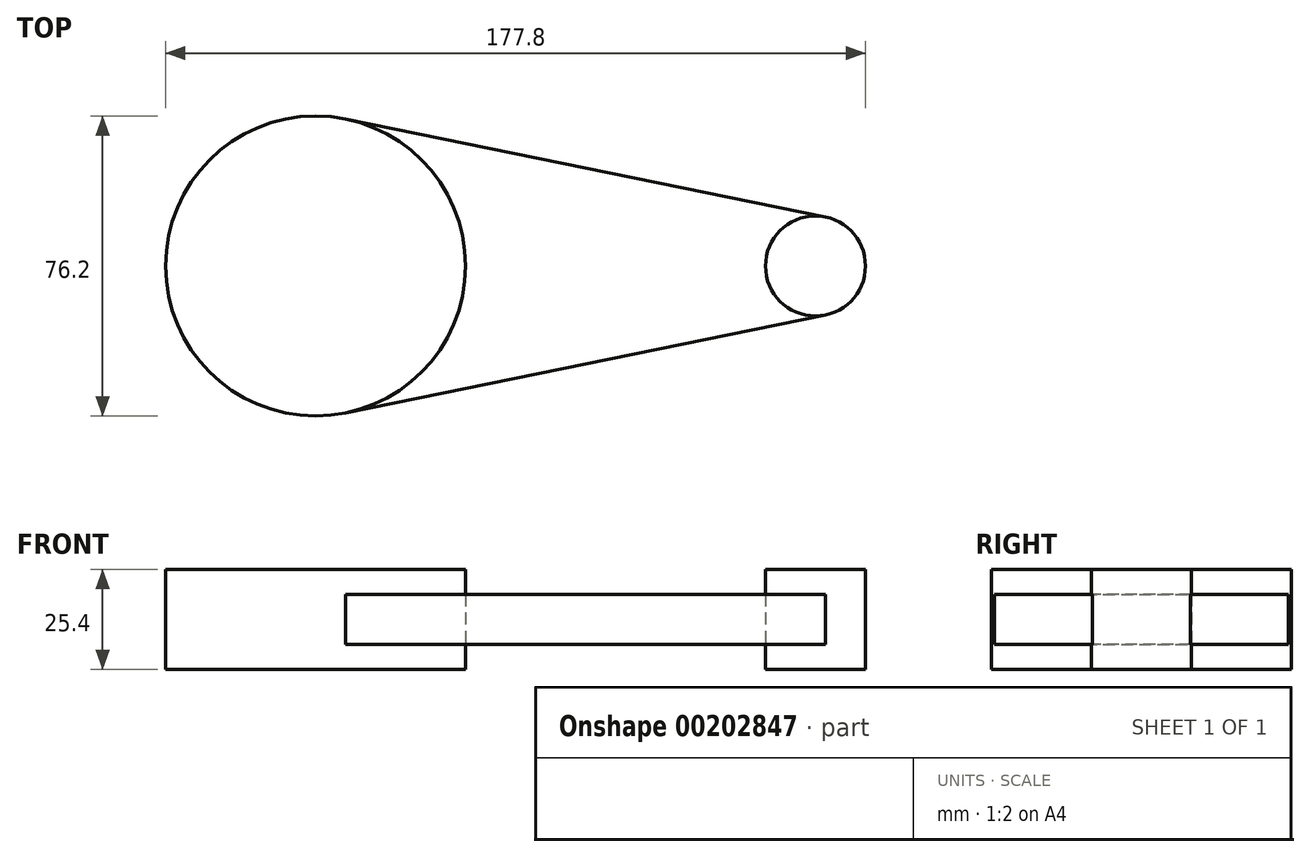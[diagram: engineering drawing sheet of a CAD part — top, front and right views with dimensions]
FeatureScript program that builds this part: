
annotation { "Feature Type Name" : "Feature", "Feature Type Description" : "" }
export const myFeature = defineFeature(function(context is Context, id is Id, definition is map)
    precondition{}
    {
        {
            var Q0;
            Q0=qCreatedBy(makeId("Top.planeOp"),FACE);
            var sketch = newSketch(context, id + "F0", { "sketchPlane" : qUnion([Q0])});
            skCircle(sketch, "E0", {"center": v(0, 0) * mm, "radius": 38.1 * mm});
            skCircle(sketch, "E1", {"center": v(127, 0) * mm, "radius": 12.7 * mm});
            skLineSegment(sketch, "E2", {"start": v(7.62, 37.33) * mm, "end": v(129.54, 12.44) * mm});
            skLineSegment(sketch, "E3", {"start": v(7.62, -37.33) * mm, "end": v(129.54, -12.44) * mm});
            skSolve(sketch);
        }
        {
            var Q0;
            {var subQ0=sQuery(id+"F0.wireOp",EDGE,"E0");var subQ1=makeQuery(id+"F0.imprint","INTERSECT",VERTEX,{"derivedFrom":[subQ0,sQuery(id+"F0.wireOp",EDGE,"E2")]});Q0=makeQuery(id+"F0.imprint","IMPRINT",FACE,{"disambiguationData":[TD([[makeQuery(id+"F0.imprint","IMPRINT",EDGE,{"disambiguationData":[TD([[subQ1,-1.0]])],"derivedFrom":subQ0}),1.0]])]});}
            extrude(context, id + "F1", {"entities" : qUnion([Q0]), "endBound" : BoundingType.SYMMETRIC, "depth" : 25.4 * mm});
        }
        {
            var Q0;
            {var subQ0=sQuery(id+"F0.wireOp",EDGE,"E1");var subQ1=makeQuery(id+"F0.imprint","INTERSECT",VERTEX,{"derivedFrom":[subQ0,sQuery(id+"F0.wireOp",EDGE,"E2")]});Q0=makeQuery(id+"F0.imprint","IMPRINT",FACE,{"disambiguationData":[TD([[makeQuery(id+"F0.imprint","IMPRINT",EDGE,{"disambiguationData":[TD([[subQ1,-1.0]])],"derivedFrom":subQ0}),1.0]])]});}
            extrude(context, id + "F2", {"entities" : qUnion([Q0]), "endBound" : BoundingType.SYMMETRIC, "depth" : 25.4 * mm});
        }
        {
            var Q0;
            {var subQ0=sQuery(id+"F0.wireOp",EDGE,"E2");Q0=makeQuery(id+"F0.imprint","IMPRINT",FACE,{"disambiguationData":[TD([[makeQuery(id+"F0.imprint","IMPRINT",EDGE,{"derivedFrom":subQ0}),-1.0]])]});}
            extrude(context, id + "F3", {"entities" : qUnion([Q0]), "endBound" : BoundingType.SYMMETRIC, "depth" : 12.7 * mm});
        }
    });
